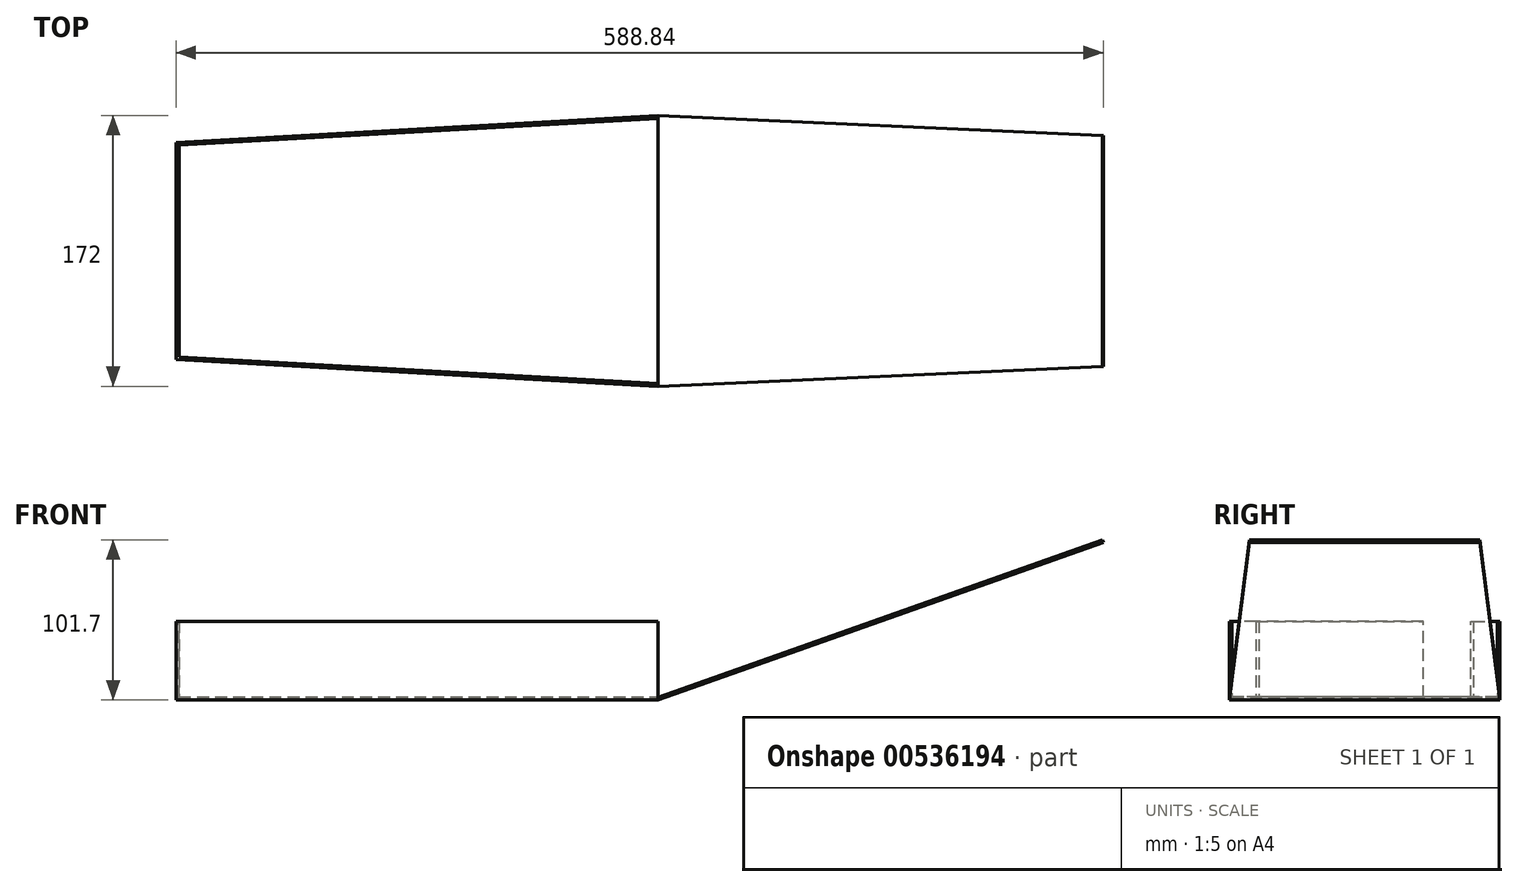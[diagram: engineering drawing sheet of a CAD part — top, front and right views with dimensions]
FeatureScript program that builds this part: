
annotation { "Feature Type Name" : "Feature", "Feature Type Description" : "" }
export const myFeature = defineFeature(function(context is Context, id is Id, definition is map)
    precondition{}
    {
        {
            var Q0;
            Q0=qCreatedBy(makeId("Top.planeOp"),FACE);
            var sketch = newSketch(context, id + "F0", { "sketchPlane" : qUnion([Q0])});
            skLineSegment(sketch, "E0", {"start": v(-306, 0) * mm, "end": v(-306, -69) * mm});
            skLineSegment(sketch, "E1", {"start": v(-306, -69) * mm, "end": v(0, -86) * mm});
            skLineSegment(sketch, "E2", {"start": v(0, -86) * mm, "end": v(300, -72.5) * mm});
            skLineSegment(sketch, "E3", {"start": v(300, -72.5) * mm, "end": v(300, 0) * mm});
            skLineSegment(sketch, "E4", {"start": v(-306, -67.2) * mm, "end": v(0, -84.2) * mm});
            skLineSegment(sketch, "E5", {"start": v(0, -84.2) * mm, "end": v(0, -86) * mm});
            skLineSegment(sketch, "E6.MirrorCS", {"start": v(0, 84.2) * mm, "end": v(0, 86) * mm});
            skLineSegment(sketch, "E7.MirrorCS", {"start": v(300, 72.5) * mm, "end": v(300, 0) * mm});
            skLineSegment(sketch, "E8.MirrorCS", {"start": v(-306, 67.2) * mm, "end": v(0, 84.2) * mm});
            skLineSegment(sketch, "E9.MirrorCS", {"start": v(-306, 69) * mm, "end": v(0, 86) * mm});
            skLineSegment(sketch, "E10.MirrorCS", {"start": v(-306, 0) * mm, "end": v(-306, 69) * mm});
            skLineSegment(sketch, "E11.MirrorCS", {"start": v(0, 86) * mm, "end": v(300, 72.5) * mm});
            skLineSegment(sketch, "E12", {"start": v(-304.2, 69.1) * mm, "end": v(-304.2, -69.1) * mm});
            skLineSegment(sketch, "E13", {"start": v(0, 86) * mm, "end": v(300, 86) * mm});
            skLineSegment(sketch, "E14", {"start": v(300, 86) * mm, "end": v(300, 72.5) * mm});
            skLineSegment(sketch, "E15", {"start": v(0, -86) * mm, "end": v(300, -86) * mm});
            skLineSegment(sketch, "E16", {"start": v(300, -86) * mm, "end": v(300, -72.5) * mm});
            skLineSegment(sketch, "E17", {"start": v(0, 86) * mm, "end": v(0, -86) * mm});
            skSolve(sketch);
        }
        {
            var Q0;
            Q0=qCreatedBy(makeId("Front.planeOp"),FACE);
            var sketch = newSketch(context, id + "F1", { "sketchPlane" : qUnion([Q0])});
            skLineSegment(sketch, "E18", {"start": v(0, 0) * mm, "end": v(282.84, 100) * mm});
            skLineSegment(sketch, "E19", {"start": v(283.04, 0) * mm, "end": v(282.84, 100) * mm});
            skLineSegment(sketch, "E20", {"start": v(0, 0) * mm, "end": v(0, 1.58) * mm});
            skLineSegment(sketch, "E21", {"start": v(0, 1.58) * mm, "end": v(282.24, 101.7) * mm});
            skLineSegment(sketch, "E22", {"start": v(282.84, 100) * mm, "end": v(282.24, 101.7) * mm});
            skArc(sketch, "E23", {"start": v(300, 0) * mm, "mid": v(285.5, 92.15) * mm, "end": v(243.39, 175.4) * mm});
            skSolve(sketch);
        }
        {
            var Q0;
            Q0=makeQuery(id+"F1.imprint","IMPRINT",FACE,{"disambiguationData":[TD([[makeQuery(id+"F1.imprint","IMPRINT",EDGE,{"derivedFrom":sQuery(id+"F1.wireOp",EDGE,"E18")}),1.0]])]});
            extrude(context, id + "F2", {"entities" : qUnion([Q0]), "endBound" : BoundingType.SYMMETRIC, "depth" : 172 * mm, "offsetDistance" : 25 * mm});
        }
        {
            var Q0;
            Q0=makeQuery(id+"F0.imprint","IMPRINT",FACE,{"disambiguationData":[TD([[makeQuery(id+"F0.imprint","IMPRINT",EDGE,{"derivedFrom":sQuery(id+"F0.wireOp",EDGE,"E2")}),-1.0]])]});
            var Q1;
            Q1=makeQuery(id+"F0.imprint","IMPRINT",FACE,{"disambiguationData":[TD([[makeQuery(id+"F0.imprint","IMPRINT",EDGE,{"derivedFrom":sQuery(id+"F0.wireOp",EDGE,"E11.MirrorCS")}),1.0]])]});
            extrude(context, id + "F3", {"entities" : qUnion([Q0, Q1]), "operationType" : NewBodyOperationType.REMOVE, "depth" : 121 * mm, "offsetDistance" : 25 * mm});
        }
        {
            var Q0;
            {var subQ0=sQuery(id+"F0.wireOp",EDGE,"E10.MirrorCS");var subQ1=sQuery(id+"F0.wireOp",EDGE,"E0");var subQ2=makeQuery(id+"F0.imprint","INTERSECT",VERTEX,{"derivedFrom":[subQ1,subQ0]});Q0=makeQuery(id+"F0.imprint","IMPRINT",FACE,{"disambiguationData":[TD([[makeQuery(id+"F0.imprint","IMPRINT",EDGE,{"disambiguationData":[TD([[subQ2,-1.0]])],"derivedFrom":subQ1}),1.0]])]});}
            var Q1;
            {var subQ0=sQuery(id+"F0.wireOp",EDGE,"E17");var subQ5=sQuery(id+"F0.wireOp",EDGE,"E4");var subQ7=makeQuery(id+"F0.imprint","INTERSECT",VERTEX,{"derivedFrom":[subQ5,subQ0]});Q1=makeQuery(id+"F0.imprint","IMPRINT",FACE,{"disambiguationData":[TD([[makeQuery(id+"F0.imprint","IMPRINT",EDGE,{"disambiguationData":[TD([[subQ7,1.0]])],"derivedFrom":subQ5}),-1.0]])]});}
            var Q2;
            {var subQ0=sQuery(id+"F0.wireOp",EDGE,"E17");var subQ1=sQuery(id+"F0.wireOp",EDGE,"E8.MirrorCS");var subQ2=makeQuery(id+"F0.imprint","INTERSECT",VERTEX,{"derivedFrom":[subQ1,subQ0]});Q2=makeQuery(id+"F0.imprint","IMPRINT",FACE,{"disambiguationData":[TD([[makeQuery(id+"F0.imprint","IMPRINT",EDGE,{"disambiguationData":[TD([[subQ2,1.0]])],"derivedFrom":subQ1}),1.0]])]});}
            var Q3;
            {var subQ0=sQuery(id+"F0.wireOp",EDGE,"E1");var subQ1=sQuery(id+"F0.wireOp",EDGE,"E0");var subQ2=makeQuery(id+"F0.imprint","INTERSECT",VERTEX,{"derivedFrom":[subQ1,subQ0]});Q3=makeQuery(id+"F0.imprint","IMPRINT",FACE,{"disambiguationData":[TD([[makeQuery(id+"F0.imprint","IMPRINT",EDGE,{"disambiguationData":[TD([[subQ2,1.0]])],"derivedFrom":subQ1}),1.0]])]});}
            var Q4;
            {var subQ0=sQuery(id+"F0.wireOp",EDGE,"E10.MirrorCS");var subQ1=sQuery(id+"F0.wireOp",EDGE,"E8.MirrorCS");var subQ2=makeQuery(id+"F0.imprint","INTERSECT",VERTEX,{"derivedFrom":[subQ1,subQ0]});Q4=makeQuery(id+"F0.imprint","IMPRINT",FACE,{"disambiguationData":[TD([[makeQuery(id+"F0.imprint","IMPRINT",EDGE,{"disambiguationData":[TD([[subQ2,-1.0]])],"derivedFrom":subQ1}),1.0]])]});}
            extrude(context, id + "F4", {"entities" : qUnion([Q0, Q1, Q2, Q3, Q4]), "operationType" : NewBodyOperationType.ADD, "depth" : 50 * mm, "offsetDistance" : 25 * mm});
        }
        {
            var Q0;
            {var subQ0=sQuery(id+"F0.wireOp",EDGE,"E17");var subQ1=sQuery(id+"F0.wireOp",EDGE,"E4");var subQ2=makeQuery(id+"F0.imprint","INTERSECT",VERTEX,{"derivedFrom":[subQ1,subQ0]});Q0=makeQuery(id+"F0.imprint","IMPRINT",FACE,{"disambiguationData":[TD([[makeQuery(id+"F0.imprint","IMPRINT",EDGE,{"disambiguationData":[TD([[subQ2,1.0]])],"derivedFrom":subQ1}),1.0]])]});}
            extrude(context, id + "F5", {"entities" : qUnion([Q0]), "depth" : 1.8 * mm, "offsetDistance" : 25 * mm});
        }
        {
            var Q0;
            Q0=makeQuery(id+"F4.opExtrude","SWEPT_FACE",FACE,{"disambiguationData":[OSD([sQuery(id+"F0.wireOp",EDGE,"E12")])]});
            var sketch = newSketch(context, id + "F6", { "sketchPlane" : qUnion([Q0])});
            skLineSegment(sketch, "E24", {"start": v(67.3, 50) * mm, "end": v(67.3, 1.8) * mm});
            skLineSegment(sketch, "E25", {"start": v(67.3, 1.8) * mm, "end": v(37.3, 1.8) * mm});
            skLineSegment(sketch, "E26", {"start": v(37.3, 1.8) * mm, "end": v(37.3, 50) * mm});
            skLineSegment(sketch, "E27", {"start": v(37.3, 50) * mm, "end": v(67.3, 50) * mm});
            skSolve(sketch);
        }
        {
            var Q0;
            Q0=makeQuery(id+"F6.imprint","IMPRINT",FACE,{"disambiguationData":[TD([[makeQuery(id+"F6.imprint","IMPRINT",EDGE,{"derivedFrom":sQuery(id+"F6.wireOp",EDGE,"E24")}),-1.0]])]});
            extrude(context, id + "F7", {"entities" : qUnion([Q0]), "operationType" : NewBodyOperationType.REMOVE, "oppositeDirection" : true, "depth" : 25 * mm, "offsetDistance" : 25 * mm});
        }
    });
